# Revit family: IS_UltraFlatS_K8190_BIM_DE
name_source: partatom
category: Plumbing Fixtures
revit_build: Autodesk Revit MEP 2015 (Build: 20140606_1530(x64)
units: mm (PartAtom-declared; Revit-internal decimal feet)

## types (5) — shared parameters
Assembly Code = C1030200
Description = ULTRA FLAT S rectangular shower tray 900x700mm
DrainSize = 90 mm  [stored 0.295276 ft]
HasTray = No
IfcExportAs = IfcSanitaryTerminalType
IfcExportType = SHOWER
ManufacturerURL = www.idealstandard.com
Material = Composite Material
Name = ULTRA FLAT S rectangular shower tray 900x700mm
NettWeight = 22,7 kg
NominalHeight = 30 mm  [stored 0.0984252 ft]
NominalLength = 900 mm  [stored 2.95276 ft]
NominalWidth = 700 mm  [stored 2.29659 ft]
ProductInformation = www.idealstandard.de/produkte
Shape = Rectangular
Size = 900x700x30
Space = Internal
SpareParts = www.idealstandard.de/ersatzteile
URL = www.idealstandard.com
Version = 1
VolumeUnits = Litres
WarrantyDurationUnit = year
zero-valued in all types: CWFU, Cost, Default Elevation, HWFU, NominalDepth, WFU

## per-type parameters (varying)
| type | Model | ModelNumber |
| K8190FR - ULTRA FLAT S rectangular shower tray 900x700mm | K8190FR | K8190FR |
| K8190FS - ULTRA FLAT S rectangular shower tray 900x700mm | K8190FS | K8190FS |
| K8190FV - ULTRA FLAT S rectangular shower tray 900x700mm | K8190FV | K8190FV |
| K8190FT - ULTRA FLAT S rectangular shower tray 900x700mm | K8190FT | K8190FT |
| K8190FU - ULTRA FLAT S rectangular shower tray 900x700mm | K8190FU | K8190FU |

note: [stored X ft] marks values corroborated as IEEE doubles in the binary element streams (Revit-internal decimal feet)

## geometry (parser evidence)
native form markers: Blend x2, Sweep x3
no freeform markers — native parametric forms only
